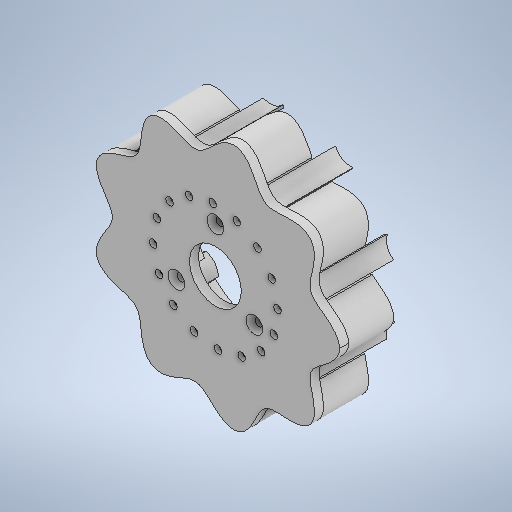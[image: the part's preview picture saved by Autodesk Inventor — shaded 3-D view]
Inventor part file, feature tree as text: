
AUTODESK INVENTOR PART (.ipt)
format: ipt  version: 2025 (Build 290162000, 162)  size: 896,512 bytes
history: native  units: mm
features: sketch x8, extrude x6, chamfer x1, other x1
ambient origin geometry x8: Origin, YZ Plane, XZ Plane, XY Plane, X Axis, Y Axis, Z Axis, Center Point
bodies: 实体1 (feature_tree)
feature tree (16):
  sketch  "草图1"  dims[d0=67.5mm d1=40.0mm]
  extrude  "拉伸1"  Depth=40.0mm
  extrude  "拉伸2"  Depth=30.0mm TaperAngle=360.0deg
  sketch  "草图2"  dims[d7=1.0mm d8=0.0mm d9=3600.0mm]
  extrude  "拉伸5"  Depth=3600.0mm TaperAngle=0.0deg
  extrude  "拉伸6"  Depth=4.0mm TaperAngle=0.0deg
  sketch  "草图4"  dims[d21=67.0mm]
  extrude  "拉伸7"  Depth=2.0mm TaperAngle=45.0deg
  chamfer  "倒角1"  Distance=96.0mm
  extrude  "拉伸8"  Depth=10.0mm
  sketch  "草图 - 环形阵列1"  dims[d2=3.4mm d3=30.0mm d5=360.0deg]
  other  "二维表达式曲线1"
  sketch  "草图 - 环形阵列2"  dims[d10=23.0mm d11=4.0mm d12=0.0mm]
  sketch  "草图3"  dims[d13=20.0mm d14=0.0mm d15=2.0mm d16=2.0mm d17=45.0deg]
  sketch  "草图 - 环形阵列3"  dims[d20=84.5mm]
  sketch  "草图 - 环形阵列5"  dims[d22=90.0mm d23=96.0mm d24=85.1mm d25=1.0mm d28=1.0mm d31=0.5mm d37=90.0mm d39=360.0deg d41=30.0mm d42=0.0mm d43=3.15mm d44=90.0mm d46=360.0deg d48=8.0mm d49=0.0mm d50=55.25mm d51=10.15mm d56=2.0mm d57=0.0mm d58=3.3mm d59=160.0mm d61=360.0deg d63=10.0mm d64=0.0mm]
